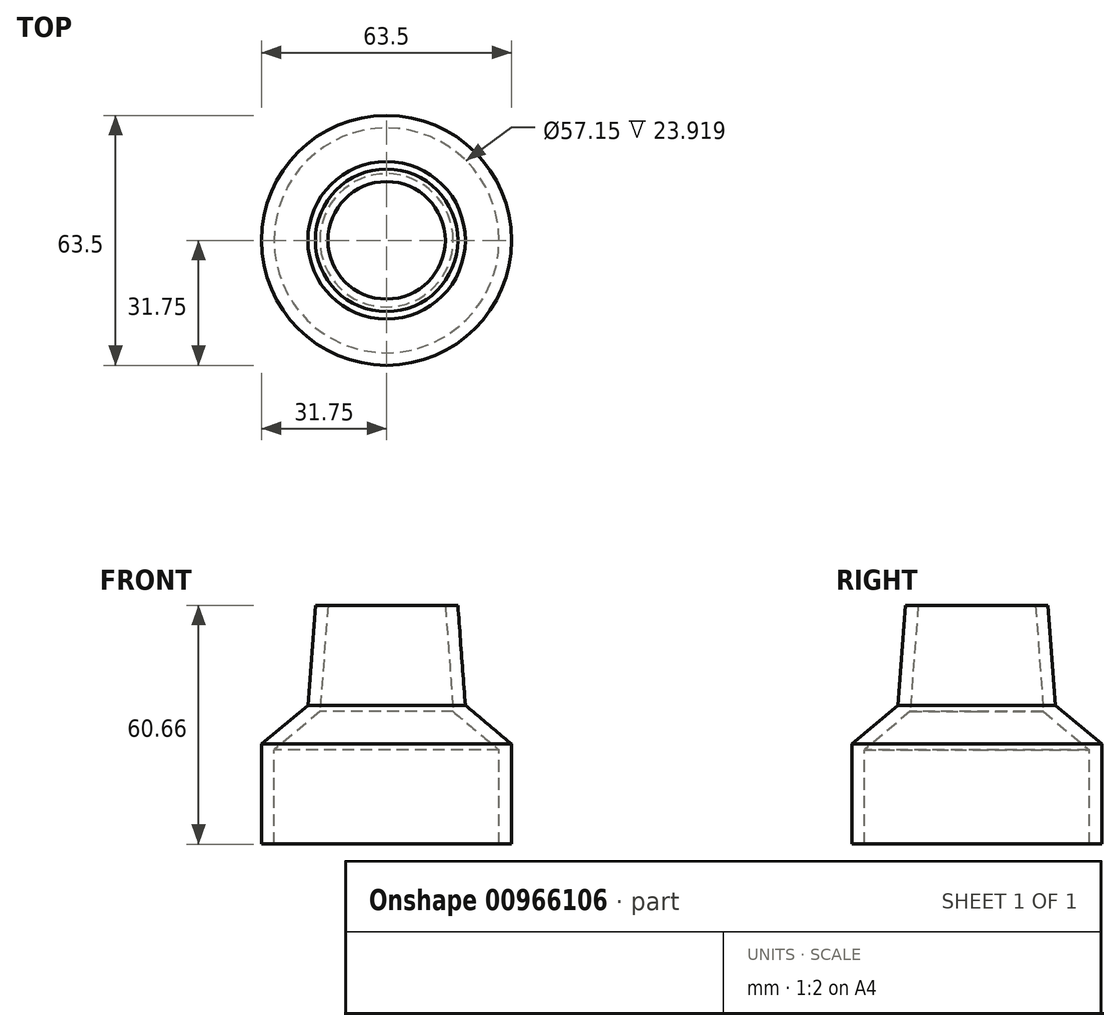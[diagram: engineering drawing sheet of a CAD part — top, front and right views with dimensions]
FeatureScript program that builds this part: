
annotation { "Feature Type Name" : "Feature", "Feature Type Description" : "" }
export const myFeature = defineFeature(function(context is Context, id is Id, definition is map)
    precondition{}
    {
        {
            var Q0;
            Q0=qCreatedBy(makeId("Front.planeOp"),FACE);
            var sketch = newSketch(context, id + "F0", { "sketchPlane" : qUnion([Q0])});
            skLineSegment(sketch, "E0", {"start": v(-18.1, 0) * mm, "end": v(-20, -25.4) * mm});
            skLineSegment(sketch, "E1", {"start": v(-20, -25.4) * mm, "end": v(-31.75, -35.26) * mm});
            skLineSegment(sketch, "E2", {"start": v(-31.75, -35.26) * mm, "end": v(-31.75, -60.66) * mm});
            skLineSegment(sketch, "E3", {"start": v(0, 0) * mm, "end": v(0, -64.35) * mm, "construction": true});
            skLineSegment(sketch, "E4", {"start": v(-19.05, -12.7) * mm, "end": v(0, -12.7) * mm, "construction": true});
            skPoint(sketch, "E4.endSnap0", {"position": v(-19.05, -12.7) * mm});
            skLineSegment(sketch, "E5.0", {"start": v(-28.57, -36.74) * mm, "end": v(-28.57, -60.66) * mm});
            skLineSegment(sketch, "E5.1", {"start": v(-16.94, -26.97) * mm, "end": v(-28.58, -36.74) * mm});
            skLineSegment(sketch, "E5.2", {"start": v(-14.91, 0) * mm, "end": v(-16.94, -26.97) * mm});
            skLineSegment(sketch, "E6", {"start": v(-18.1, 0) * mm, "end": v(-14.91, 0) * mm});
            skLineSegment(sketch, "E7", {"start": v(-31.75, -60.66) * mm, "end": v(-28.57, -60.66) * mm});
            skSolve(sketch);
        }
        {
            var Q0;
            Q0 = qSketchRegion(id + "F0", true);
            var Q1;
            Q1=sQuery(id+"F0.wireOp",EDGE,"E3");
            revolve(context, id + "F1", {"surfaceOperationType" : NewSurfaceOperationType.NEW, "entities" : qUnion([Q0]), "axis" : qUnion([Q1]), "revolveType" : RevolveType.FULL});
        }
    });
